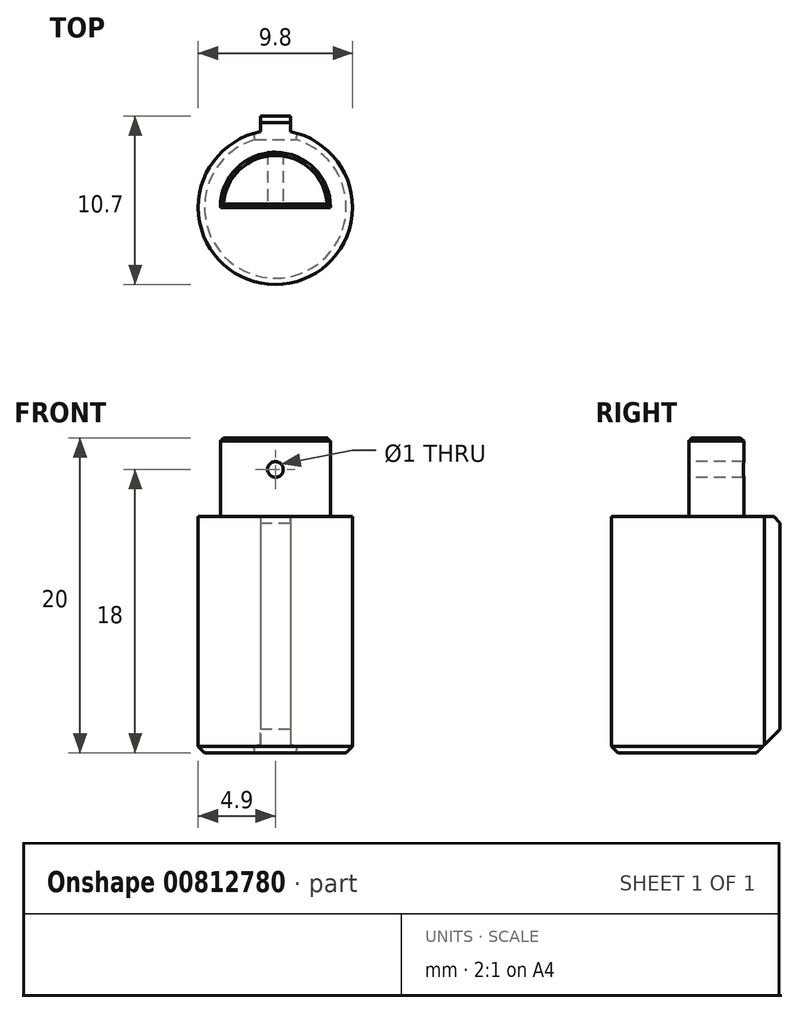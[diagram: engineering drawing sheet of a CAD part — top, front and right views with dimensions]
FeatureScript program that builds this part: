
annotation { "Feature Type Name" : "Feature", "Feature Type Description" : "" }
export const myFeature = defineFeature(function(context is Context, id is Id, definition is map)
    precondition{}
    {
        {
            var Q0;
            Q0=qCreatedBy(makeId("Front.planeOp"),FACE);
            var sketch = newSketch(context, id + "F0", { "sketchPlane" : qUnion([Q0])});
            skLineSegment(sketch, "E0", {"start": v(0, 42.37) * mm, "end": v(0, -13.34) * mm, "construction": true});
            skSolve(sketch);
        }
        {
            var Q0;
            Q0=qCreatedBy(makeId("Top.planeOp"),FACE);
            var sketch = newSketch(context, id + "F1", { "sketchPlane" : qUnion([Q0])});
            skCircle(sketch, "E1", {"center": v(0, 0) * mm, "radius": 4.9 * mm});
            skSolve(sketch);
        }
        {
            var Q0;
            Q0=makeQuery(id+"F1.imprint","IMPRINT",FACE,{"disambiguationData":[TD([[makeQuery(id+"F1.imprint","IMPRINT",EDGE,{"derivedFrom":sQuery(id+"F1.wireOp",EDGE,"E1")}),1.0]])]});
            extrude(context, id + "F2", {"entities" : qUnion([Q0]), "depth" : 5 * mm, "offsetDistance" : 25 * mm, "hasSecondDirection" : true, "secondDirectionOppositeDirection" : true, "secondDirectionDepth" : 15 * mm});
        }
        {
            var Q0;
            Q0=qCreatedBy(makeId("Top.planeOp"),FACE);
            var sketch = newSketch(context, id + "F3", { "sketchPlane" : qUnion([Q0])});
            skArc(sketch, "E2", {"start": v(3.5, 0) * mm, "mid": v(0, 3.5) * mm, "end": v(-3.5, 0) * mm});
            skLineSegment(sketch, "E3", {"start": v(-3.5, 0) * mm, "end": v(3.5, 0) * mm});
            skCircle(sketch, "E4", {"center": v(0, 0) * mm, "radius": 4.9 * mm});
            skSolve(sketch);
        }
        {
            var Q0;
            Q0=qCreatedBy(makeId("Front.planeOp"),FACE);
            cPlane(context, id + "F4", {"entities" : qUnion([Q0]), "cplaneType" : CPlaneType.OFFSET, "offset" : 5.8 * mm, "oppositeDirection" : true, "width" : 150 * mm, "height" : 150 * mm});
        }
        {
            var Q0;
            Q0=qCreatedBy(id+"F4.planeOp",FACE);
            var sketch = newSketch(context, id + "F5", { "sketchPlane" : qUnion([Q0])});
            skLineSegment(sketch, "E5.bottom", {"start": v(-0.95, 0) * mm, "end": v(0.95, 0) * mm});
            skLineSegment(sketch, "E5.top", {"start": v(-0.95, -15) * mm, "end": v(0.95, -15) * mm});
            skLineSegment(sketch, "E5.left", {"start": v(-0.95, 0) * mm, "end": v(-0.95, -15) * mm});
            skLineSegment(sketch, "E5.right", {"start": v(0.95, 0) * mm, "end": v(0.95, -15) * mm});
            skSolve(sketch);
        }
        {
            var Q0;
            Q0=makeQuery(id+"F5.imprint","IMPRINT",FACE,{"disambiguationData":[TD([[makeQuery(id+"F5.imprint","IMPRINT",EDGE,{"derivedFrom":sQuery(id+"F5.wireOp",EDGE,"E5.bottom")}),-1.0]])]});
            extrude(context, id + "F6", {"entities" : qUnion([Q0]), "operationType" : NewBodyOperationType.ADD, "endBound" : BoundingType.UP_TO_NEXT, "depth" : 25 * mm, "offsetDistance" : 25 * mm});
        }
        {
            var Q0;
            Q0=makeQuery(id+"F3.imprint","IMPRINT",FACE,{"disambiguationData":[TD([[makeQuery(id+"F3.imprint","IMPRINT",EDGE,{"derivedFrom":sQuery(id+"F3.wireOp",EDGE,"E2")}),-1.0]])]});
            extrude(context, id + "F7", {"entities" : qUnion([Q0]), "operationType" : NewBodyOperationType.REMOVE, "endBound" : BoundingType.THROUGH_ALL, "depth" : 25 * mm, "offsetDistance" : 25 * mm});
        }
        {
            var Q0;
            Q0=makeQuery(id+"F7.boolean.opBoolean","COPY",FACE,{"derivedFrom":makeQuery(id+"F7.opExtrude","SWEPT_FACE",FACE,{"disambiguationData":[OSD([sQuery(id+"F3.wireOp",EDGE,"E3")])]})});
            var sketch = newSketch(context, id + "F8", { "sketchPlane" : qUnion([Q0])});
            skCircle(sketch, "E6", {"center": v(0, 3) * mm, "radius": 0.5 * mm});
            skSolve(sketch);
        }
        {
            var Q0;
            Q0=makeQuery(id+"F8.imprint","IMPRINT",FACE,{"disambiguationData":[TD([[makeQuery(id+"F8.imprint","IMPRINT",EDGE,{"derivedFrom":sQuery(id+"F8.wireOp",EDGE,"E6")}),1.0]])]});
            extrude(context, id + "F9", {"entities" : qUnion([Q0]), "operationType" : NewBodyOperationType.REMOVE, "endBound" : BoundingType.THROUGH_ALL, "oppositeDirection" : true, "depth" : 25 * mm, "offsetDistance" : 25 * mm});
        }
        {
            var Q0;
            Q0=makeQuery(id+"F2.opExtrude","CAP_FACE",FACE,{"disambiguationData":[OSD([sQuery(id+"F1.wireOp",EDGE,"E1")])],"isStart":false});
            chamfer(context, id + "F10", {"entities" : qUnion([Q0]), "width" : .2 * mm, "tangentPropagation" : true});
        }
        {
            var Q0;
            {var subQ1=sQuery(id+"F1.wireOp",EDGE,"E1");Q0=makeQuery(id+"F1f1suCUSjg3Mzx_1.1.F6.boolean.opBoolean","SPLIT",EDGE,{"disambiguationData":[TD([makeQuery(id+"F6.opExtrude","SWEPT_FACE",FACE,{"disambiguationData":[OSD([sQuery(id+"F5.wireOp",EDGE,"E5.right")])]})])],"derivedFrom":makeQuery(id+"F2.opExtrude","CAP_EDGE",EDGE,{"disambiguationData":[OSD([subQ1])],"isStart":true})});}
            var Q1;
            {var subQ1=sQuery(id+"F1.wireOp",EDGE,"E1");Q1=makeQuery(id+"F1f1suCUSjg3Mzx_1.1.F6.boolean.opBoolean","SPLIT",EDGE,{"disambiguationData":[TD([makeQuery(id+"F6.opExtrude","SWEPT_FACE",FACE,{"disambiguationData":[OSD([sQuery(id+"F5.wireOp",EDGE,"E5.left")])]})])],"derivedFrom":makeQuery(id+"F2.opExtrude","CAP_EDGE",EDGE,{"disambiguationData":[OSD([subQ1])],"isStart":true})});}
            chamfer(context, id + "F11", {"entities" : qUnion([Q0, Q1]), "width" : .4 * mm, "tangentPropagation" : true});
        }
        {
            var Q0;
            Q0=makeQuery(id+"F1f1suCUSjg3Mzx_1.1.F6.opExtrude","CAP_EDGE",EDGE,{"disambiguationData":[OSD([sQuery(id+"F5.wireOp",EDGE,"E5.top")])],"isStart":true});
            var Q1;
            Q1=makeQuery(id+"F6.opExtrude","CAP_EDGE",EDGE,{"disambiguationData":[OSD([sQuery(id+"F5.wireOp",EDGE,"E5.top")])],"isStart":true});
            chamfer(context, id + "F12", {"entities" : qUnion([Q0, Q1]), "width" : 1.5 * mm, "tangentPropagation" : true});
        }
        {
            var Q0;
            Q0=makeQuery(id+"F1f1suCUSjg3Mzx_1.1.F6.opExtrude","CAP_EDGE",EDGE,{"disambiguationData":[OSD([sQuery(id+"F5.wireOp",EDGE,"E5.bottom")])],"isStart":true});
            var Q1;
            Q1=makeQuery(id+"F6.opExtrude","CAP_EDGE",EDGE,{"disambiguationData":[OSD([sQuery(id+"F5.wireOp",EDGE,"E5.bottom")])],"isStart":true});
            chamfer(context, id + "F13", {"entities" : qUnion([Q0, Q1]), "width" : .4 * mm, "tangentPropagation" : true});
        }
    });
